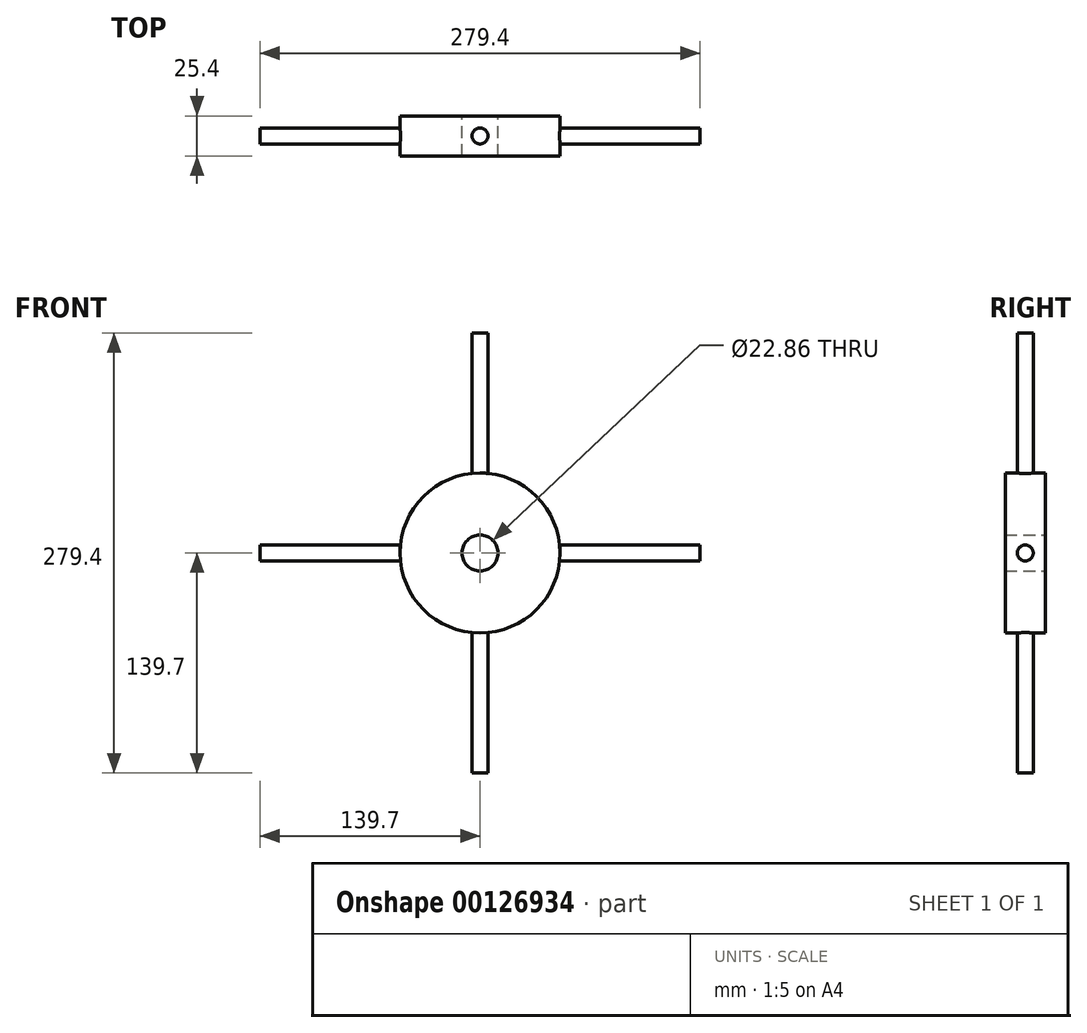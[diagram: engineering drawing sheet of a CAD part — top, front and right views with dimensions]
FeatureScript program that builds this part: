
annotation { "Feature Type Name" : "Feature", "Feature Type Description" : "" }
export const myFeature = defineFeature(function(context is Context, id is Id, definition is map)
    precondition{}
    {
        {
            var Q0;
            Q0=qCreatedBy(makeId("Front.planeOp"),FACE);
            var sketch = newSketch(context, id + "F0", { "sketchPlane" : qUnion([Q0])});
            skCircle(sketch, "E0", {"center": v(0, 0) * mm, "radius": 50.8 * mm});
            skSolve(sketch);
        }
        {
            var Q0;
            Q0=makeQuery(id+"F0.imprint","IMPRINT",FACE,{"disambiguationData":[TD([[makeQuery(id+"F0.imprint","IMPRINT",EDGE,{"derivedFrom":sQuery(id+"F0.wireOp",EDGE,"E0")}),1.0]])]});
            extrude(context, id + "F1", {"entities" : qUnion([Q0]), "depth" : 25.4 * mm});
        }
        {
            var Q0;
            Q0=qCreatedBy(makeId("Right.planeOp"),FACE);
            var sketch = newSketch(context, id + "F2", { "sketchPlane" : qUnion([Q0])});
            skCircle(sketch, "E1", {"center": v(-12.7, 0) * mm, "radius": 5.08 * mm});
            skLineSegment(sketch, "E2", {"start": v(0, 0) * mm, "end": v(-25.4, 0) * mm, "construction": true});
            skSolve(sketch);
        }
        {
            var Q0;
            Q0=qSketchRegion(id+"F2",true);
            extrude(context, id + "F3", {"entities" : qUnion([Q0]), "operationType" : NewBodyOperationType.ADD, "depth" : 139.7 * mm, "hasSecondDirection" : true, "secondDirectionOppositeDirection" : true, "secondDirectionDepth" : 139.7 * mm});
        }
        {
            var Q0;
            Q0=qCreatedBy(makeId("Top.planeOp"),FACE);
            var sketch = newSketch(context, id + "F4", { "sketchPlane" : qUnion([Q0])});
            skCircle(sketch, "E3", {"center": v(0, -12.7) * mm, "radius": 5.08 * mm});
            skSolve(sketch);
        }
        {
            var Q0;
            Q0=qSketchRegion(id+"F4",true);
            extrude(context, id + "F5", {"entities" : qUnion([Q0]), "operationType" : NewBodyOperationType.ADD, "depth" : 139.7 * mm, "hasSecondDirection" : true, "secondDirectionOppositeDirection" : true, "secondDirectionDepth" : 139.7 * mm});
        }
        {
            var Q0;
            Q0=qCreatedBy(makeId("Front.planeOp"),FACE);
            var sketch = newSketch(context, id + "F6", { "sketchPlane" : qUnion([Q0])});
            skCircle(sketch, "E4", {"center": v(0, 0) * mm, "radius": 11.43 * mm});
            skSolve(sketch);
        }
        {
            var Q0;
            Q0=qSketchRegion(id+"F6",true);
            extrude(context, id + "F7", {"entities" : qUnion([Q0]), "operationType" : NewBodyOperationType.REMOVE, "depth" : 27.94 * mm});
        }
    });
